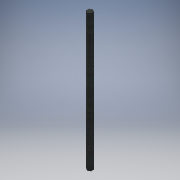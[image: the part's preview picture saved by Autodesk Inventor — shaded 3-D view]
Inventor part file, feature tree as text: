
AUTODESK INVENTOR PART (.ipt)
format: ipt  version: 2016 (Build 200138000, 138)  size: 93,184 bytes
history: native  units: in
note: dims shown in document units (in); Inventor stores cm internally (conversion verified against a paired STEP export)
features: extrude x1, sketch x1
ambient origin geometry x8: Origin, YZ Plane, XZ Plane, XY Plane, X Axis, Y Axis, Z Axis, Center Point
bodies: Solid1 (feature_tree)
feature tree (2):
  extrude  "Extrusion1"  Depth=14.0in TaperAngle=0.0deg
  sketch  "Sketch1"  dims[d0=0.5in d1=14.0in d2=0.0in]
